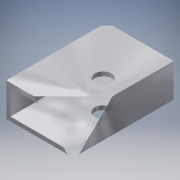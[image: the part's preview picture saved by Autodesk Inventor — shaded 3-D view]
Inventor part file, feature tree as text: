
AUTODESK INVENTOR PART (.ipt)
format: ipt  version: 2016 (Build 200138000, 138)  size: 115,712 bytes
history: native  units: in
note: dims shown in document units (in); Inventor stores cm internally (conversion verified against a paired STEP export)
features: sketch x2, extrude x1, hole x1
ambient origin geometry x8: Origin, YZ Plane, XZ Plane, XY Plane, X Axis, Y Axis, Z Axis, Center Point
bodies: Solid1 (feature_tree)
feature tree (4):
  extrude  "Extrusion1"  Depth=1.0in
  hole  "Hole1"  [1 undecoded]
  sketch  "Sketch1"  dims[d0=2.0in d1=1.0in]
  sketch  "Sketch2"  dims[d2=0.125in d3=3.0in d4=0.0in d6=1.5in d7=1.125in d8=0.75in d9=0.375in d10=0.25in d11=0.5635in d12=1.0in d13=0.8108in d14=1.0in]
note: 1 required parameter value undecoded (feature->parameter linkage not recoverable at this tier; creation-order binding heuristic only, values carry confidence <= 0.55)
